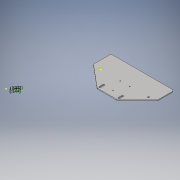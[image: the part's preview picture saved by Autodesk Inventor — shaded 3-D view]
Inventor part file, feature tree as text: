
AUTODESK INVENTOR PART (.ipt)
format: ipt  version: 2016 (Build 200138000, 138)  size: 207,872 bytes
history: native  units: in
note: dims shown in document units (in); Inventor stores cm internally (conversion verified against a paired STEP export)
features: sketch x8, extrude x4, hole x2
ambient origin geometry x8: Origin, YZ Plane, XZ Plane, XY Plane, X Axis, Y Axis, Z Axis, Center Point
bodies: Solid1 (feature_tree)
feature tree (14):
  extrude  "Extrusion1"  Depth=8.5in
  hole  "Hole1"  [1 undecoded]
  extrude  "Extrusion3"  Depth=3.1102in
  extrude  "Extrusion4"  Depth=0.25in
  extrude  "Extrusion5"  Depth=1.0236in
  sketch  "Sketch9"  dims[d24=0.2953in]
  hole  "Hole2"  [1 undecoded]
  sketch  "Sketch11"  dims[d40=3.8881in d43=1.0in d44=0.0in d45=1.75in d47=1.75in d48=1.75in d49=1.75in d50=2.382in d52=2.5591in d53=0.6398in d54=0.6398in d55=2.382in d58=2.0472in d62=1.2795in d64=0.1181in d65=0.75in d66=0.375in d67=0.25in d68=0.5635in d69=1.0in d70=0.8108in d72=0.2362in d76=0.236in d77=0.492in d78=0.236in d79=0.492in d80=1.0in d81=0.0in d82=0.236in d83=0.492in d84=0.236in d85=0.492in d86=1.0in d87=0.0in d88=0.2362in d93=0.2953in d95=2.3746in d96=2.07in d99=135.0deg d100=0.25in d101=0.25in d102=0.25in d103=0.25in d104=0.962in d125=0.0in d126=0.5445in d127=0.5445in d128=0.2722in d129=0.2722in]
  sketch  "Sketch1"  dims[d0=8.5in d1=6.0in]
  sketch  "Sketch2"  dims[d2=0.125in d3=0.0in d4=5.6831in]
  sketch  "Sketch3"  dims[d5=1.0236in d7=3.1102in]
  sketch  "Sketch5"  dims[d12=0.2362in d13=0.75in d14=0.375in d15=0.25in d16=0.5635in d17=1.0in d18=0.8108in d19=1.0768in]
  sketch  "Sketch7"  dims[d20=3.1102in d21=1.0236in]
  sketch  "Sketch8"  dims[d22=3.124in d23=7.5728in]
note: 2 required parameter values undecoded (feature->parameter linkage not recoverable at this tier; creation-order binding heuristic only, values carry confidence <= 0.55)
